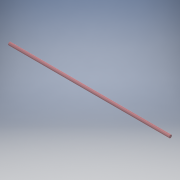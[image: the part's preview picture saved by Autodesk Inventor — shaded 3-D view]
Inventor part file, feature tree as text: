
AUTODESK INVENTOR PART (.ipt)
format: ipt  version: 2016 (Build 200138000, 138)  size: 104,448 bytes
history: native  units: mm
features: extrude x1, sketch x1
ambient origin geometry x8: Origin, YZ Plane, XZ Plane, XY Plane, X Axis, Y Axis, Z Axis, Center Point
bodies: Solid1 (feature_tree)
feature tree (2):
  extrude  "Extrusion1"  Depth=165.0mm TaperAngle=0.0deg
  sketch  "Sketch2"  dims[d0=3.0mm d1=165.0mm d2=0.0mm]
